# Revit family: 16-100-220_Simplified
name_source: partatom
category: Generic Models
units: mm (PartAtom-declared; Revit-internal decimal feet)

## family parameters
Always vertical = No
Can host rebar = No
Cut with Voids When Loaded = No
Part Type = Normal
Room Calculation Point = No
Round Connector Dimension = Use Diameter
Shared = No
Work Plane-Based = Yes

## types (1)
- Type 1
    Artnr = 16-200-045
    Artnr_Simplified = 16-100-210
    CheckedDate = -
    CheckedDate_Simplified = -
    Default Elevation = 1219.2 mm  [stored 4 ft]
    Description_Simplified = Multifunksjonelt treningsapparat
    Number = 13464
    Number_Simplified = 13464
    PartName = 16-200-045
    PartName_Simplified = Multifunksjonelt treningsapparat
    Revision = 0
    Revision_Simplified = 0

note: [stored X ft] marks values corroborated as IEEE doubles in the binary element streams (Revit-internal decimal feet)

## geometry (parser evidence)
native form markers: Sweep x2
no freeform markers — native parametric forms only
